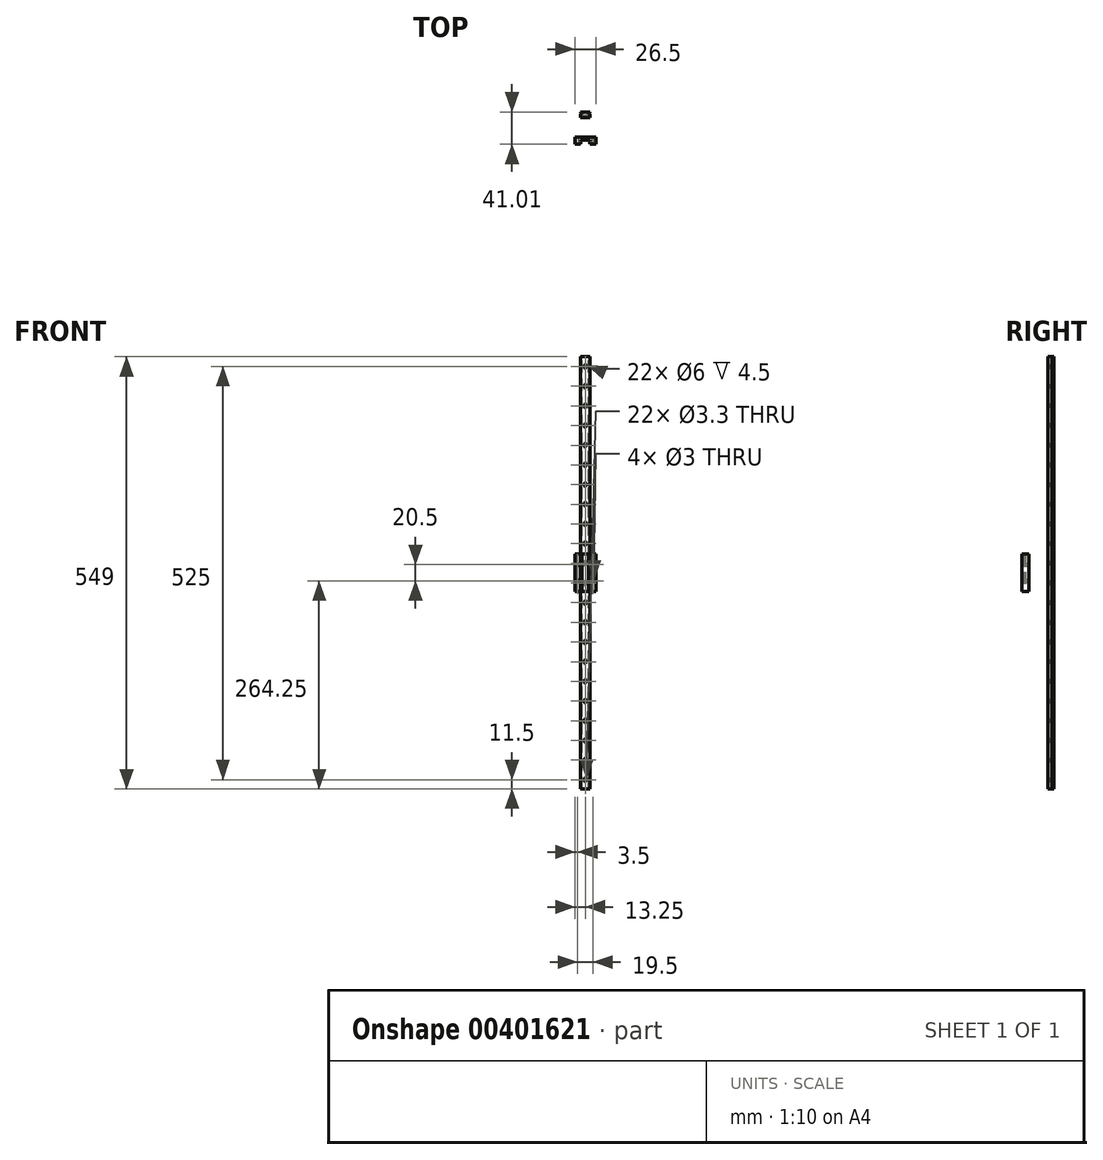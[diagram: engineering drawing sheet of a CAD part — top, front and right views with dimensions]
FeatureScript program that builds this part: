
annotation { "Feature Type Name" : "Feature", "Feature Type Description" : "" }
export const myFeature = defineFeature(function(context is Context, id is Id, definition is map)
    precondition{}
    {
        {
            var Q0;
            Q0=qCreatedBy(makeId("Front.planeOp"),FACE);
            var sketch = newSketch(context, id + "F0", { "sketchPlane" : qUnion([Q0])});
            skLineSegment(sketch, "E0.bottom", {"start": v(-6, 274.5) * mm, "end": v(6, 274.5) * mm});
            skLineSegment(sketch, "E0.top", {"start": v(-6, -274.5) * mm, "end": v(6, -274.5) * mm});
            skLineSegment(sketch, "E0.left", {"start": v(-6, 274.5) * mm, "end": v(-6, -274.5) * mm});
            skLineSegment(sketch, "E0.right", {"start": v(6, 274.5) * mm, "end": v(6, -274.5) * mm});
            skPoint(sketch, "E0.middle", {"position": v(0, 0) * mm});
            skSolve(sketch);
        }
        {
            var Q0;
            Q0=qSketchRegion(id+"F0",true);
            extrude(context, id + "F1", {"entities" : qUnion([Q0]), "depth" : 7.4 * mm, "symmetric" : true});
        }
        {
            var Q0;
            Q0=makeQuery(id+"F1.opExtrude","SWEPT_FACE",FACE,{"disambiguationData":[OSD([sQuery(id+"F0.wireOp",EDGE,"E0.bottom")])]});
            var sketch = newSketch(context, id + "F2", { "sketchPlane" : qUnion([Q0])});
            skLineSegment(sketch, "E1", {"start": v(-6, 2.7) * mm, "end": v(-4, 1.7) * mm});
            skLineSegment(sketch, "E2", {"start": v(-4, 1.7) * mm, "end": v(-6, 1.03) * mm});
            skLineSegment(sketch, "E3.MirrorCS", {"start": v(6, 2.7) * mm, "end": v(4, 1.7) * mm});
            skLineSegment(sketch, "E4.MirrorCS", {"start": v(4, 1.7) * mm, "end": v(6, 1.03) * mm});
            skSolve(sketch);
        }
        {
            var Q0;
            {var subQ0=sQuery(id+"F2.wireOp",EDGE,"E1");Q0=makeQuery(id+"F2.imprint","IMPRINT",FACE,{"disambiguationData":[TD([[makeQuery(id+"F2.imprint","IMPRINT",EDGE,{"derivedFrom":subQ0}),-1.0]])]});}
            var Q1;
            {var subQ0=sQuery(id+"F2.wireOp",EDGE,"E3.MirrorCS");Q1=makeQuery(id+"F2.imprint","IMPRINT",FACE,{"disambiguationData":[TD([[makeQuery(id+"F2.imprint","IMPRINT",EDGE,{"derivedFrom":subQ0}),1.0]])]});}
            extrude(context, id + "F3", {"entities" : qUnion([Q0, Q1]), "operationType" : NewBodyOperationType.REMOVE, "endBound" : BoundingType.THROUGH_ALL, "oppositeDirection" : true, "depth" : 100 * mm});
        }
        {
            var Q0;
            Q0=makeQuery(id+"F1.opExtrude","CAP_FACE",FACE,{"disambiguationData":[OSD([sQuery(id+"F0.wireOp",EDGE,"E0.bottom"),sQuery(id+"F0.wireOp",EDGE,"E0.top"),sQuery(id+"F0.wireOp",EDGE,"E0.left"),sQuery(id+"F0.wireOp",EDGE,"E0.right")])],"isStart":true});
            var sketch = newSketch(context, id + "F4", { "sketchPlane" : qUnion([Q0])});
            skCircle(sketch, "E5", {"center": v(0, 262) * mm, "radius": 3 * mm});
            skPoint(sketch, "E6", {"position": v(0, 274.5) * mm});
            skCircle(sketch, "E7.0.1.0", {"center": v(0, 237) * mm, "radius": 3 * mm});
            skCircle(sketch, "E7.0.2.0", {"center": v(0, 212) * mm, "radius": 3 * mm});
            skCircle(sketch, "E7.0.3.0", {"center": v(0, 187) * mm, "radius": 3 * mm});
            skCircle(sketch, "E7.0.4.0", {"center": v(0, 162) * mm, "radius": 3 * mm});
            skCircle(sketch, "E7.0.5.0", {"center": v(0, 137) * mm, "radius": 3 * mm});
            skCircle(sketch, "E7.0.6.0", {"center": v(0, 112) * mm, "radius": 3 * mm});
            skCircle(sketch, "E7.0.7.0", {"center": v(0, 87) * mm, "radius": 3 * mm});
            skCircle(sketch, "E7.0.8.0", {"center": v(0, 62) * mm, "radius": 3 * mm});
            skCircle(sketch, "E7.0.9.0", {"center": v(0, 37) * mm, "radius": 3 * mm});
            skCircle(sketch, "E7.0.10.0", {"center": v(0, 12) * mm, "radius": 3 * mm});
            skCircle(sketch, "E7.0.11.0", {"center": v(0, -13) * mm, "radius": 3 * mm});
            skCircle(sketch, "E7.0.12.0", {"center": v(0, -38) * mm, "radius": 3 * mm});
            skCircle(sketch, "E7.0.13.0", {"center": v(0, -63) * mm, "radius": 3 * mm});
            skCircle(sketch, "E7.0.14.0", {"center": v(0, -88) * mm, "radius": 3 * mm});
            skCircle(sketch, "E7.0.15.0", {"center": v(0, -113) * mm, "radius": 3 * mm});
            skCircle(sketch, "E7.0.16.0", {"center": v(0, -138) * mm, "radius": 3 * mm});
            skCircle(sketch, "E7.0.17.0", {"center": v(0, -163) * mm, "radius": 3 * mm});
            skCircle(sketch, "E7.0.18.0", {"center": v(0, -188) * mm, "radius": 3 * mm});
            skCircle(sketch, "E7.0.19.0", {"center": v(0, -213) * mm, "radius": 3 * mm});
            skCircle(sketch, "E7.0.20.0", {"center": v(0, -238) * mm, "radius": 3 * mm});
            skCircle(sketch, "E7.0.21.0", {"center": v(0, -263) * mm, "radius": 3 * mm});
            skLineSegment(sketch, "E7.direction1", {"start": v(0, 262) * mm, "end": v(25, 262) * mm, "construction": true});
            skLineSegment(sketch, "E7.direction2", {"start": v(0, 262) * mm, "end": v(0, 237) * mm, "construction": true});
            skSolve(sketch);
        }
        {
            var Q0;
            Q0=qSketchRegion(id+"F4",true);
            extrude(context, id + "F5", {"entities" : qUnion([Q0]), "operationType" : NewBodyOperationType.REMOVE, "oppositeDirection" : true, "depth" : 4.5 * mm});
        }
        {
            var Q0;
            Q0=makeQuery(id+"F1.opExtrude","CAP_FACE",FACE,{"disambiguationData":[OSD([sQuery(id+"F0.wireOp",EDGE,"E0.bottom"),sQuery(id+"F0.wireOp",EDGE,"E0.top"),sQuery(id+"F0.wireOp",EDGE,"E0.left"),sQuery(id+"F0.wireOp",EDGE,"E0.right")])],"isStart":false});
            var sketch = newSketch(context, id + "F6", { "sketchPlane" : qUnion([Q0])});
            skCircle(sketch, "E8", {"center": v(0, 262) * mm, "radius": 1.65 * mm});
            skCircle(sketch, "E9.0.1.0", {"center": v(0, 237) * mm, "radius": 1.65 * mm});
            skCircle(sketch, "E9.0.2.0", {"center": v(0, 212) * mm, "radius": 1.65 * mm});
            skCircle(sketch, "E9.0.3.0", {"center": v(0, 187) * mm, "radius": 1.65 * mm});
            skCircle(sketch, "E9.0.4.0", {"center": v(0, 162) * mm, "radius": 1.65 * mm});
            skCircle(sketch, "E9.0.5.0", {"center": v(0, 137) * mm, "radius": 1.65 * mm});
            skCircle(sketch, "E9.0.6.0", {"center": v(0, 112) * mm, "radius": 1.65 * mm});
            skCircle(sketch, "E9.0.7.0", {"center": v(0, 87) * mm, "radius": 1.65 * mm});
            skCircle(sketch, "E9.0.8.0", {"center": v(0, 62) * mm, "radius": 1.65 * mm});
            skCircle(sketch, "E9.0.9.0", {"center": v(0, 37) * mm, "radius": 1.65 * mm});
            skCircle(sketch, "E9.0.10.0", {"center": v(0, 12) * mm, "radius": 1.65 * mm});
            skCircle(sketch, "E9.0.11.0", {"center": v(0, -13) * mm, "radius": 1.65 * mm});
            skCircle(sketch, "E9.0.12.0", {"center": v(0, -38) * mm, "radius": 1.65 * mm});
            skCircle(sketch, "E9.0.13.0", {"center": v(0, -63) * mm, "radius": 1.65 * mm});
            skCircle(sketch, "E9.0.14.0", {"center": v(0, -88) * mm, "radius": 1.65 * mm});
            skCircle(sketch, "E9.0.15.0", {"center": v(0, -113) * mm, "radius": 1.65 * mm});
            skCircle(sketch, "E9.0.16.0", {"center": v(0, -138) * mm, "radius": 1.65 * mm});
            skCircle(sketch, "E9.0.17.0", {"center": v(0, -163) * mm, "radius": 1.65 * mm});
            skCircle(sketch, "E9.0.18.0", {"center": v(0, -188) * mm, "radius": 1.65 * mm});
            skCircle(sketch, "E9.0.19.0", {"center": v(0, -213) * mm, "radius": 1.65 * mm});
            skCircle(sketch, "E9.0.20.0", {"center": v(0, -238) * mm, "radius": 1.65 * mm});
            skCircle(sketch, "E9.0.21.0", {"center": v(0, -263) * mm, "radius": 1.65 * mm});
            skLineSegment(sketch, "E9.direction1", {"start": v(0, 262) * mm, "end": v(25, 262) * mm, "construction": true});
            skLineSegment(sketch, "E9.direction2", {"start": v(0, 262) * mm, "end": v(0, 237) * mm, "construction": true});
            skSolve(sketch);
        }
        {
            var Q0;
            Q0=qSketchRegion(id+"F6",true);
            extrude(context, id + "F7", {"entities" : qUnion([Q0]), "operationType" : NewBodyOperationType.REMOVE, "oppositeDirection" : true, "depth" : 25 * mm});
        }
        {
            var Q0;
            Q0=qCreatedBy(makeId("Top.planeOp"),FACE);
            var sketch = newSketch(context, id + "F8", { "sketchPlane" : qUnion([Q0])});
            skLineSegment(sketch, "E10.bottom", {"start": v(-13.25, -28.3) * mm, "end": v(13.25, -28.3) * mm});
            skLineSegment(sketch, "E10.top", {"start": v(-13.25, -37.3) * mm, "end": v(-6, -37.3) * mm});
            skLineSegment(sketch, "E10.left", {"start": v(-13.25, -28.3) * mm, "end": v(-13.25, -37.3) * mm});
            skLineSegment(sketch, "E10.right", {"start": v(13.25, -28.3) * mm, "end": v(13.25, -37.3) * mm});
            skLineSegment(sketch, "E11.bottom", {"start": v(-6, -32.3) * mm, "end": v(6, -32.3) * mm});
            skLineSegment(sketch, "E12", {"start": v(-6, -33.3) * mm, "end": v(-4.16, -34.3) * mm});
            skLineSegment(sketch, "E13", {"start": v(-4.16, -34.3) * mm, "end": v(-6, -34.85) * mm});
            skLineSegment(sketch, "E14", {"start": v(-6, -32.3) * mm, "end": v(-6, -33.3) * mm});
            skLineSegment(sketch, "E15", {"start": v(-6, -34.85) * mm, "end": v(-6, -37.3) * mm});
            skLineSegment(sketch, "E16.MirrorCS", {"start": v(6, -33.3) * mm, "end": v(4.16, -34.3) * mm});
            skLineSegment(sketch, "E17.MirrorCS", {"start": v(4.16, -34.3) * mm, "end": v(6, -34.85) * mm});
            skLineSegment(sketch, "E18", {"start": v(6, -33.3) * mm, "end": v(6, -32.3) * mm});
            skLineSegment(sketch, "E19", {"start": v(6, -34.85) * mm, "end": v(6, -37.3) * mm});
            skLineSegment(sketch, "E20.trimOffspring", {"start": v(6, -37.3) * mm, "end": v(13.25, -37.3) * mm});
            skSolve(sketch);
        }
        {
            var Q0;
            Q0=makeQuery(id+"F8.imprint","IMPRINT",FACE,{"disambiguationData":[TD([[makeQuery(id+"F8.imprint","IMPRINT",EDGE,{"derivedFrom":sQuery(id+"F8.wireOp",EDGE,"E10.bottom")}),-1.0]])]});
            extrude(context, id + "F9", {"entities" : qUnion([Q0]), "depth" : 47.5 * mm, "symmetric" : true});
        }
        {
            var Q0;
            Q0=makeQuery(id+"F9.opExtrude","SWEPT_FACE",FACE,{"disambiguationData":[OSD([sQuery(id+"F8.wireOp",EDGE,"E10.bottom")])]});
            var sketch = newSketch(context, id + "F10", { "sketchPlane" : qUnion([Q0])});
            skCircle(sketch, "E21", {"center": v(9.75, -10.25) * mm, "radius": 1.5 * mm});
            skCircle(sketch, "E22.MirrorC", {"center": v(9.75, 10.25) * mm, "radius": 1.5 * mm});
            skCircle(sketch, "E23.MirrorC", {"center": v(-9.75, 10.25) * mm, "radius": 1.5 * mm});
            skCircle(sketch, "E24.MirrorC", {"center": v(-9.75, -10.25) * mm, "radius": 1.5 * mm});
            skSolve(sketch);
        }
        {
            var Q0;
            Q0=qSketchRegion(id+"F10",true);
            extrude(context, id + "F11", {"entities" : qUnion([Q0]), "operationType" : NewBodyOperationType.REMOVE, "oppositeDirection" : true, "depth" : 25 * mm});
        }
    });
